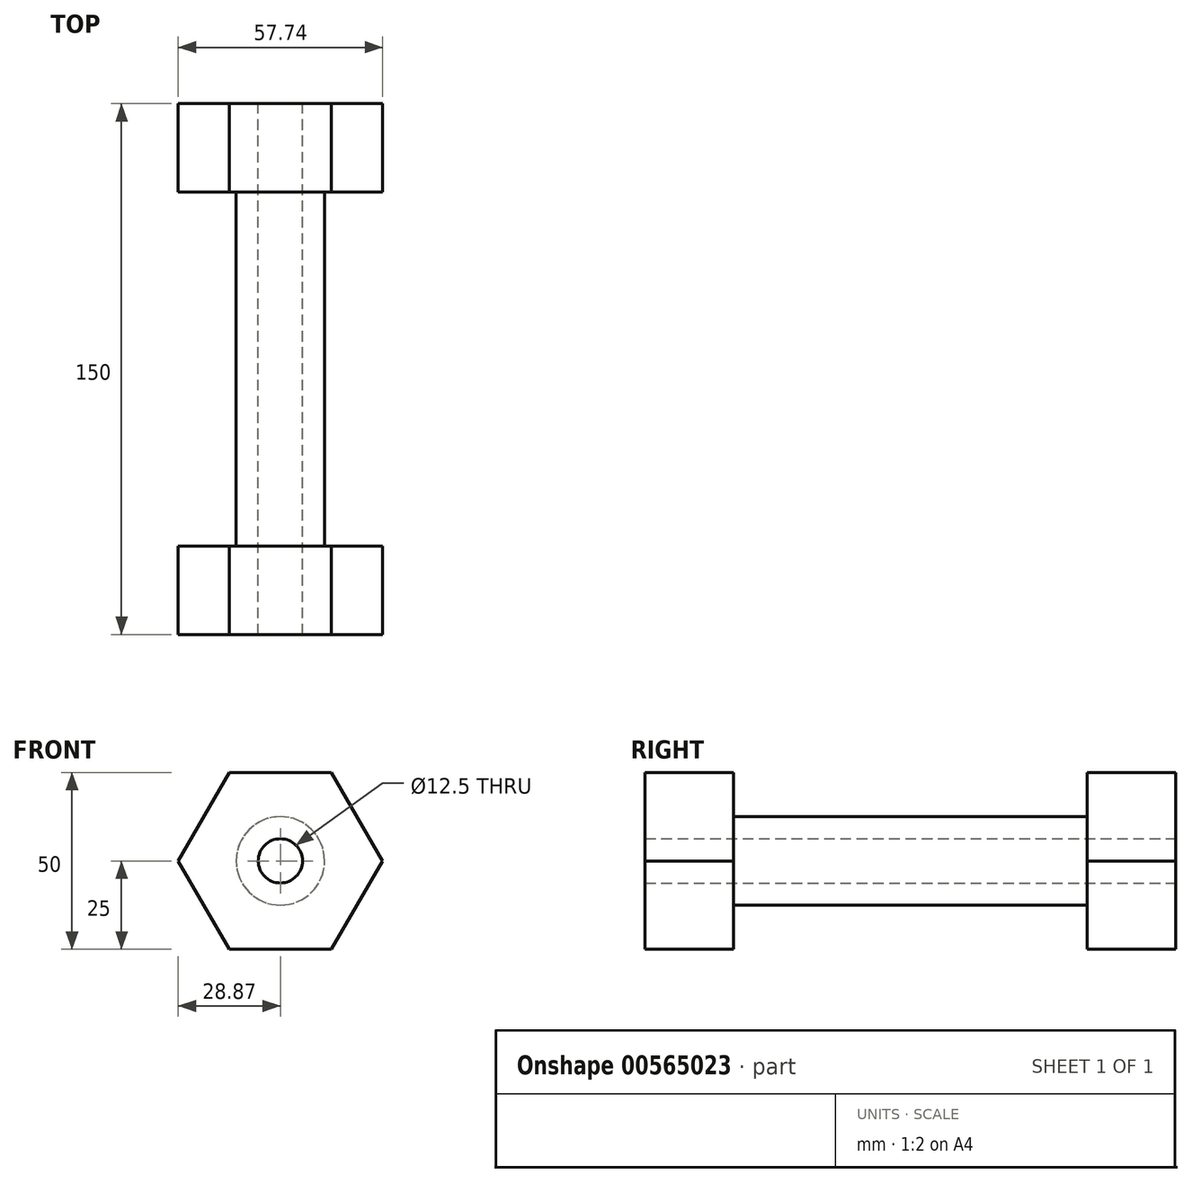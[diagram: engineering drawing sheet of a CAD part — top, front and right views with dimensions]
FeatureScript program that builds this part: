
annotation { "Feature Type Name" : "Feature", "Feature Type Description" : "" }
export const myFeature = defineFeature(function(context is Context, id is Id, definition is map)
    precondition{}
    {
        {
            var Q0;
            Q0=qCreatedBy(makeId("Front.planeOp"),FACE);
            var sketch = newSketch(context, id + "F0", { "sketchPlane" : qUnion([Q0])});
            skCircle(sketch, "E0.cCircle", {"center": v(0, 0) * mm, "radius": 25 * mm, "construction": true});
            skLineSegment(sketch, "E0.0", {"start": v(14.43, -25) * mm, "end": v(-14.43, -25) * mm});
            skLineSegment(sketch, "E0.1", {"start": v(-14.43, -25) * mm, "end": v(-28.87, 0) * mm});
            skLineSegment(sketch, "E0.2", {"start": v(-28.87, 0) * mm, "end": v(-14.43, 25) * mm});
            skLineSegment(sketch, "E0.3", {"start": v(-14.43, 25) * mm, "end": v(14.43, 25) * mm});
            skLineSegment(sketch, "E0.4", {"start": v(14.43, 25) * mm, "end": v(28.87, 0) * mm});
            skLineSegment(sketch, "E0.5", {"start": v(28.87, 0) * mm, "end": v(14.43, -25) * mm});
            skPoint(sketch, "E0.0.midPoint", {"position": v(0, -25) * mm});
            skCircle(sketch, "E1", {"center": v(0, 0) * mm, "radius": 12.5 * mm});
            skCircle(sketch, "E2", {"center": v(0, 0) * mm, "radius": 6.25 * mm});
            skSolve(sketch);
        }
        {
            var Q0;
            Q0 = qSketchRegion(id + "F0", true);
            extrude(context, id + "F1", {"entities" : qUnion([Q0]), "depth" : 25 * mm, "offsetDistance" : 25 * mm});
        }
        {
            var Q0;
            Q0=makeQuery(id+"F1.opExtrude","CAP_FACE",FACE,{"disambiguationData":[OSD([sQuery(id+"F0.wireOp",EDGE,"E0.0"),sQuery(id+"F0.wireOp",EDGE,"E0.1"),sQuery(id+"F0.wireOp",EDGE,"E0.2"),sQuery(id+"F0.wireOp",EDGE,"E0.3"),sQuery(id+"F0.wireOp",EDGE,"E0.4"),sQuery(id+"F0.wireOp",EDGE,"E0.5"),sQuery(id+"F0.wireOp",EDGE,"E1")])],"isStart":false});
            var sketch = newSketch(context, id + "F2", { "sketchPlane" : qUnion([Q0])});
            skCircle(sketch, "E3.0", {"center": v(0, 0) * mm, "radius": 12.5 * mm});
            skCircle(sketch, "E4.0", {"center": v(0, 0) * mm, "radius": 6.25 * mm});
            skSolve(sketch);
        }
        {
            var Q0;
            Q0 = qSketchRegion(id + "F2", true);
            extrude(context, id + "F3", {"entities" : qUnion([Q0]), "depth" : 50 * mm, "offsetDistance" : 25 * mm});
        }
        {
            var Q0;
            Q0=makeQuery(id+"F0.imprint","IMPRINT",FACE,{"disambiguationData":[TD([[makeQuery(id+"F0.imprint","IMPRINT",EDGE,{"derivedFrom":sQuery(id+"F0.wireOp",EDGE,"E0.0")}),-1.0]])]});
            var sketch = newSketch(context, id + "F4", { "sketchPlane" : qUnion([Q0])});
            skCircle(sketch, "E5.0", {"center": v(0, 0) * mm, "radius": 12.5 * mm});
            skCircle(sketch, "E6.0", {"center": v(0, 0) * mm, "radius": 6.25 * mm});
            skSolve(sketch);
        }
        {
            var Q0;
            Q0 = qSketchRegion(id + "F4", true);
            extrude(context, id + "F5", {"entities" : qUnion([Q0]), "depth" : 25 * mm, "offsetDistance" : 25 * mm});
        }
        {
            var Q0;
            Q0=makeQuery(id+"F3.opExtrude","SWEPT_BODY",BODY,{"disambiguationData":[OSD([sQuery(id+"F2.wireOp",EDGE,"E3.0"),sQuery(id+"F2.wireOp",EDGE,"E4.0")])]});
            var Q1;
            Q1=makeQuery(id+"F1.opExtrude","SWEPT_BODY",BODY,{"disambiguationData":[OSD([sQuery(id+"F0.wireOp",EDGE,"E0.0"),sQuery(id+"F0.wireOp",EDGE,"E0.1"),sQuery(id+"F0.wireOp",EDGE,"E0.2"),sQuery(id+"F0.wireOp",EDGE,"E0.3"),sQuery(id+"F0.wireOp",EDGE,"E0.4"),sQuery(id+"F0.wireOp",EDGE,"E0.5"),sQuery(id+"F0.wireOp",EDGE,"E1")])]});
            var Q2;
            Q2=makeQuery(id+"F5.opExtrude","SWEPT_BODY",BODY,{"disambiguationData":[OSD([sQuery(id+"F4.wireOp",EDGE,"E5.0"),sQuery(id+"F4.wireOp",EDGE,"E6.0")])]});
            var Q3;
            Q3=makeQuery(id+"F3.opExtrude","CAP_FACE",FACE,{"disambiguationData":[OSD([sQuery(id+"F2.wireOp",EDGE,"E3.0"),sQuery(id+"F2.wireOp",EDGE,"E4.0")])],"isStart":false});
            mirror(context, id + "F6", {"operationType" : NewBodyOperationType.ADD, "entities" : qUnion([Q0, Q1, Q2]), "mirrorPlane" : qUnion([Q3])});
        }
    });
